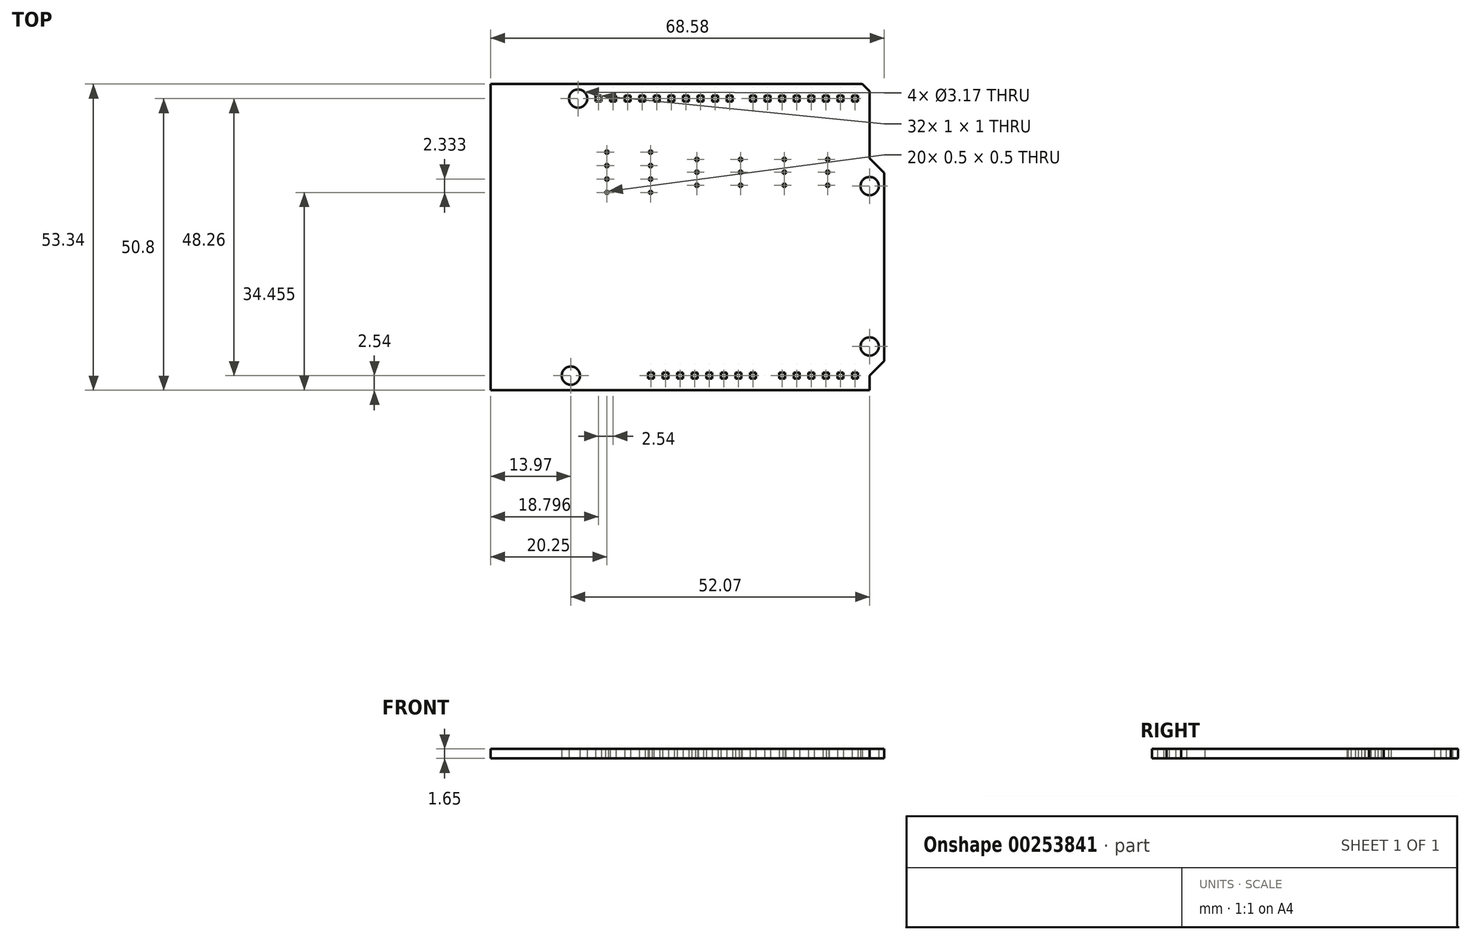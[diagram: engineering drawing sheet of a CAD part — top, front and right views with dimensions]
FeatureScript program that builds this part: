
annotation { "Feature Type Name" : "Feature", "Feature Type Description" : "" }
export const myFeature = defineFeature(function(context is Context, id is Id, definition is map)
    precondition{}
    {
        {
            var Q0;
            Q0=qCreatedBy(makeId("Top.planeOp"),FACE);
            var sketch = newSketch(context, id + "F0", { "sketchPlane" : qUnion([Q0])});
            skLineSegment(sketch, "E0", {"start": v(0, 0) * mm, "end": v(0, 53.34) * mm});
            skLineSegment(sketch, "E1", {"start": v(0, 53.34) * mm, "end": v(64.77, 53.34) * mm});
            skLineSegment(sketch, "E2", {"start": v(66.04, 52.07) * mm, "end": v(66.04, 40.39) * mm});
            skLineSegment(sketch, "E3", {"start": v(68.58, 37.85) * mm, "end": v(68.58, 5.08) * mm});
            skLineSegment(sketch, "E4", {"start": v(66.04, 0) * mm, "end": v(0, 0) * mm});
            skLineSegment(sketch, "E5", {"start": v(66.04, 40.39) * mm, "end": v(68.58, 37.85) * mm});
            skLineSegment(sketch, "E6", {"start": v(68.58, 5.08) * mm, "end": v(66.04, 2.54) * mm});
            skLineSegment(sketch, "E7", {"start": v(66.04, 2.54) * mm, "end": v(66.04, 0) * mm});
            skPoint(sketch, "E8.orphan", {"position": v(68.58, 0) * mm});
            skLineSegment(sketch, "E9", {"start": v(64.77, 53.34) * mm, "end": v(66.04, 52.07) * mm});
            skCircle(sketch, "E10", {"center": v(15.24, 50.8) * mm, "radius": 1.59 * mm});
            skCircle(sketch, "E11", {"center": v(66.04, 35.56) * mm, "radius": 1.59 * mm});
            skCircle(sketch, "E12", {"center": v(13.97, 2.54) * mm, "radius": 1.59 * mm});
            skCircle(sketch, "E13", {"center": v(66.04, 7.62) * mm, "radius": 1.59 * mm});
            skLineSegment(sketch, "E14.bottom", {"start": v(63, 3.04) * mm, "end": v(64, 3.04) * mm});
            skLineSegment(sketch, "E14.top", {"start": v(63, 2.04) * mm, "end": v(64, 2.04) * mm});
            skLineSegment(sketch, "E14.left", {"start": v(63, 3.04) * mm, "end": v(63, 2.04) * mm});
            skLineSegment(sketch, "E14.right", {"start": v(64, 3.04) * mm, "end": v(64, 2.04) * mm});
            skLineSegment(sketch, "E15", {"start": v(66.04, 2.54) * mm, "end": v(0, 2.54) * mm, "construction": true});
            skLineSegment(sketch, "E16.1.0.0", {"start": v(60.46, 3.04) * mm, "end": v(61.46, 3.04) * mm});
            skLineSegment(sketch, "E16.1.0.1", {"start": v(60.46, 3.04) * mm, "end": v(60.46, 2.04) * mm});
            skLineSegment(sketch, "E16.1.0.2", {"start": v(60.46, 2.04) * mm, "end": v(61.46, 2.04) * mm});
            skLineSegment(sketch, "E16.1.0.3", {"start": v(61.46, 3.04) * mm, "end": v(61.46, 2.04) * mm});
            skLineSegment(sketch, "E16.2.0.0", {"start": v(57.92, 3.04) * mm, "end": v(58.92, 3.04) * mm});
            skLineSegment(sketch, "E16.2.0.1", {"start": v(57.92, 3.04) * mm, "end": v(57.92, 2.04) * mm});
            skLineSegment(sketch, "E16.2.0.2", {"start": v(57.92, 2.04) * mm, "end": v(58.92, 2.04) * mm});
            skLineSegment(sketch, "E16.2.0.3", {"start": v(58.92, 3.04) * mm, "end": v(58.92, 2.04) * mm});
            skLineSegment(sketch, "E16.3.0.0", {"start": v(55.38, 3.04) * mm, "end": v(56.38, 3.04) * mm});
            skLineSegment(sketch, "E16.3.0.1", {"start": v(55.38, 3.04) * mm, "end": v(55.38, 2.04) * mm});
            skLineSegment(sketch, "E16.3.0.2", {"start": v(55.38, 2.04) * mm, "end": v(56.38, 2.04) * mm});
            skLineSegment(sketch, "E16.3.0.3", {"start": v(56.38, 3.04) * mm, "end": v(56.38, 2.04) * mm});
            skLineSegment(sketch, "E16.4.0.0", {"start": v(52.84, 3.04) * mm, "end": v(53.84, 3.04) * mm});
            skLineSegment(sketch, "E16.4.0.1", {"start": v(52.84, 3.04) * mm, "end": v(52.84, 2.04) * mm});
            skLineSegment(sketch, "E16.4.0.2", {"start": v(52.84, 2.04) * mm, "end": v(53.84, 2.04) * mm});
            skLineSegment(sketch, "E16.4.0.3", {"start": v(53.84, 3.04) * mm, "end": v(53.84, 2.04) * mm});
            skLineSegment(sketch, "E16.5.0.0", {"start": v(50.3, 3.04) * mm, "end": v(51.3, 3.04) * mm});
            skLineSegment(sketch, "E16.5.0.1", {"start": v(50.3, 3.04) * mm, "end": v(50.3, 2.04) * mm});
            skLineSegment(sketch, "E16.5.0.2", {"start": v(50.3, 2.04) * mm, "end": v(51.3, 2.04) * mm});
            skLineSegment(sketch, "E16.5.0.3", {"start": v(51.3, 3.04) * mm, "end": v(51.3, 2.04) * mm});
            skLineSegment(sketch, "E16.direction1", {"start": v(63, 3.04) * mm, "end": v(60.46, 3.04) * mm, "construction": true});
            skLineSegment(sketch, "E17.bottom", {"start": v(45.22, 3.04) * mm, "end": v(46.22, 3.04) * mm});
            skLineSegment(sketch, "E17.top", {"start": v(45.22, 2.04) * mm, "end": v(46.22, 2.04) * mm});
            skLineSegment(sketch, "E17.left", {"start": v(45.22, 3.04) * mm, "end": v(45.22, 2.04) * mm});
            skLineSegment(sketch, "E17.right", {"start": v(46.22, 3.04) * mm, "end": v(46.22, 2.04) * mm});
            skLineSegment(sketch, "E18.1.0.0", {"start": v(42.68, 3.04) * mm, "end": v(43.68, 3.04) * mm});
            skLineSegment(sketch, "E18.1.0.1", {"start": v(42.68, 3.04) * mm, "end": v(42.68, 2.04) * mm});
            skLineSegment(sketch, "E18.1.0.2", {"start": v(42.68, 2.04) * mm, "end": v(43.68, 2.04) * mm});
            skLineSegment(sketch, "E18.1.0.3", {"start": v(43.68, 3.04) * mm, "end": v(43.68, 2.04) * mm});
            skLineSegment(sketch, "E18.2.0.0", {"start": v(40.14, 3.04) * mm, "end": v(41.14, 3.04) * mm});
            skLineSegment(sketch, "E18.2.0.1", {"start": v(40.14, 3.04) * mm, "end": v(40.14, 2.04) * mm});
            skLineSegment(sketch, "E18.2.0.2", {"start": v(40.14, 2.04) * mm, "end": v(41.14, 2.04) * mm});
            skLineSegment(sketch, "E18.2.0.3", {"start": v(41.14, 3.04) * mm, "end": v(41.14, 2.04) * mm});
            skLineSegment(sketch, "E18.3.0.0", {"start": v(37.6, 3.04) * mm, "end": v(38.6, 3.04) * mm});
            skLineSegment(sketch, "E18.3.0.1", {"start": v(37.6, 3.04) * mm, "end": v(37.6, 2.04) * mm});
            skLineSegment(sketch, "E18.3.0.2", {"start": v(37.6, 2.04) * mm, "end": v(38.6, 2.04) * mm});
            skLineSegment(sketch, "E18.3.0.3", {"start": v(38.6, 3.04) * mm, "end": v(38.6, 2.04) * mm});
            skLineSegment(sketch, "E18.4.0.0", {"start": v(35.06, 3.04) * mm, "end": v(36.06, 3.04) * mm});
            skLineSegment(sketch, "E18.4.0.1", {"start": v(35.06, 3.04) * mm, "end": v(35.06, 2.04) * mm});
            skLineSegment(sketch, "E18.4.0.2", {"start": v(35.06, 2.04) * mm, "end": v(36.06, 2.04) * mm});
            skLineSegment(sketch, "E18.4.0.3", {"start": v(36.06, 3.04) * mm, "end": v(36.06, 2.04) * mm});
            skLineSegment(sketch, "E18.5.0.0", {"start": v(32.52, 3.04) * mm, "end": v(33.52, 3.04) * mm});
            skLineSegment(sketch, "E18.5.0.1", {"start": v(32.52, 3.04) * mm, "end": v(32.52, 2.04) * mm});
            skLineSegment(sketch, "E18.5.0.2", {"start": v(32.52, 2.04) * mm, "end": v(33.52, 2.04) * mm});
            skLineSegment(sketch, "E18.5.0.3", {"start": v(33.52, 3.04) * mm, "end": v(33.52, 2.04) * mm});
            skLineSegment(sketch, "E18.6.0.0", {"start": v(29.98, 3.04) * mm, "end": v(30.98, 3.04) * mm});
            skLineSegment(sketch, "E18.6.0.1", {"start": v(29.98, 3.04) * mm, "end": v(29.98, 2.04) * mm});
            skLineSegment(sketch, "E18.6.0.2", {"start": v(29.98, 2.04) * mm, "end": v(30.98, 2.04) * mm});
            skLineSegment(sketch, "E18.6.0.3", {"start": v(30.98, 3.04) * mm, "end": v(30.98, 2.04) * mm});
            skLineSegment(sketch, "E18.7.0.0", {"start": v(27.44, 3.04) * mm, "end": v(28.44, 3.04) * mm});
            skLineSegment(sketch, "E18.7.0.1", {"start": v(27.44, 3.04) * mm, "end": v(27.44, 2.04) * mm});
            skLineSegment(sketch, "E18.7.0.2", {"start": v(27.44, 2.04) * mm, "end": v(28.44, 2.04) * mm});
            skLineSegment(sketch, "E18.7.0.3", {"start": v(28.44, 3.04) * mm, "end": v(28.44, 2.04) * mm});
            skLineSegment(sketch, "E18.direction1", {"start": v(45.22, 3.04) * mm, "end": v(42.68, 3.04) * mm, "construction": true});
            skLineSegment(sketch, "E19", {"start": v(66.04, 50.8) * mm, "end": v(0, 50.8) * mm, "construction": true});
            skLineSegment(sketch, "E20.bottom", {"start": v(63, 51.3) * mm, "end": v(64, 51.3) * mm});
            skLineSegment(sketch, "E20.top", {"start": v(63, 50.3) * mm, "end": v(64, 50.3) * mm});
            skLineSegment(sketch, "E20.left", {"start": v(63, 51.3) * mm, "end": v(63, 50.3) * mm});
            skLineSegment(sketch, "E20.right", {"start": v(64, 51.3) * mm, "end": v(64, 50.3) * mm});
            skLineSegment(sketch, "E21.1.0.0", {"start": v(60.46, 51.3) * mm, "end": v(60.46, 50.3) * mm});
            skLineSegment(sketch, "E21.1.0.1", {"start": v(60.46, 51.3) * mm, "end": v(61.46, 51.3) * mm});
            skLineSegment(sketch, "E21.1.0.2", {"start": v(61.46, 51.3) * mm, "end": v(61.46, 50.3) * mm});
            skLineSegment(sketch, "E21.1.0.3", {"start": v(60.46, 50.3) * mm, "end": v(61.46, 50.3) * mm});
            skLineSegment(sketch, "E21.2.0.0", {"start": v(57.92, 51.3) * mm, "end": v(57.92, 50.3) * mm});
            skLineSegment(sketch, "E21.2.0.1", {"start": v(57.92, 51.3) * mm, "end": v(58.92, 51.3) * mm});
            skLineSegment(sketch, "E21.2.0.2", {"start": v(58.92, 51.3) * mm, "end": v(58.92, 50.3) * mm});
            skLineSegment(sketch, "E21.2.0.3", {"start": v(57.92, 50.3) * mm, "end": v(58.92, 50.3) * mm});
            skLineSegment(sketch, "E21.3.0.0", {"start": v(55.38, 51.3) * mm, "end": v(55.38, 50.3) * mm});
            skLineSegment(sketch, "E21.3.0.1", {"start": v(55.38, 51.3) * mm, "end": v(56.38, 51.3) * mm});
            skLineSegment(sketch, "E21.3.0.2", {"start": v(56.38, 51.3) * mm, "end": v(56.38, 50.3) * mm});
            skLineSegment(sketch, "E21.3.0.3", {"start": v(55.38, 50.3) * mm, "end": v(56.38, 50.3) * mm});
            skLineSegment(sketch, "E21.4.0.0", {"start": v(52.84, 51.3) * mm, "end": v(52.84, 50.3) * mm});
            skLineSegment(sketch, "E21.4.0.1", {"start": v(52.84, 51.3) * mm, "end": v(53.84, 51.3) * mm});
            skLineSegment(sketch, "E21.4.0.2", {"start": v(53.84, 51.3) * mm, "end": v(53.84, 50.3) * mm});
            skLineSegment(sketch, "E21.4.0.3", {"start": v(52.84, 50.3) * mm, "end": v(53.84, 50.3) * mm});
            skLineSegment(sketch, "E21.5.0.0", {"start": v(50.3, 51.3) * mm, "end": v(50.3, 50.3) * mm});
            skLineSegment(sketch, "E21.5.0.1", {"start": v(50.3, 51.3) * mm, "end": v(51.3, 51.3) * mm});
            skLineSegment(sketch, "E21.5.0.2", {"start": v(51.3, 51.3) * mm, "end": v(51.3, 50.3) * mm});
            skLineSegment(sketch, "E21.5.0.3", {"start": v(50.3, 50.3) * mm, "end": v(51.3, 50.3) * mm});
            skLineSegment(sketch, "E21.6.0.0", {"start": v(47.76, 51.3) * mm, "end": v(47.76, 50.3) * mm});
            skLineSegment(sketch, "E21.6.0.1", {"start": v(47.76, 51.3) * mm, "end": v(48.76, 51.3) * mm});
            skLineSegment(sketch, "E21.6.0.2", {"start": v(48.76, 51.3) * mm, "end": v(48.76, 50.3) * mm});
            skLineSegment(sketch, "E21.6.0.3", {"start": v(47.76, 50.3) * mm, "end": v(48.76, 50.3) * mm});
            skLineSegment(sketch, "E21.7.0.0", {"start": v(45.22, 51.3) * mm, "end": v(45.22, 50.3) * mm});
            skLineSegment(sketch, "E21.7.0.1", {"start": v(45.22, 51.3) * mm, "end": v(46.22, 51.3) * mm});
            skLineSegment(sketch, "E21.7.0.2", {"start": v(46.22, 51.3) * mm, "end": v(46.22, 50.3) * mm});
            skLineSegment(sketch, "E21.7.0.3", {"start": v(45.22, 50.3) * mm, "end": v(46.22, 50.3) * mm});
            skLineSegment(sketch, "E21.direction1", {"start": v(63, 50.3) * mm, "end": v(60.46, 50.3) * mm, "construction": true});
            skLineSegment(sketch, "E22.bottom", {"start": v(41.16, 51.3) * mm, "end": v(42.16, 51.3) * mm});
            skLineSegment(sketch, "E22.top", {"start": v(41.16, 50.3) * mm, "end": v(42.16, 50.3) * mm});
            skLineSegment(sketch, "E22.left", {"start": v(41.16, 51.3) * mm, "end": v(41.16, 50.3) * mm});
            skLineSegment(sketch, "E22.right", {"start": v(42.16, 51.3) * mm, "end": v(42.16, 50.3) * mm});
            skLineSegment(sketch, "E23.1.0.0", {"start": v(38.62, 51.3) * mm, "end": v(39.62, 51.3) * mm});
            skLineSegment(sketch, "E23.1.0.1", {"start": v(38.62, 51.3) * mm, "end": v(38.62, 50.3) * mm});
            skLineSegment(sketch, "E23.1.0.2", {"start": v(38.62, 50.3) * mm, "end": v(39.62, 50.3) * mm});
            skLineSegment(sketch, "E23.1.0.3", {"start": v(39.62, 51.3) * mm, "end": v(39.62, 50.3) * mm});
            skLineSegment(sketch, "E23.2.0.0", {"start": v(36.08, 51.3) * mm, "end": v(37.08, 51.3) * mm});
            skLineSegment(sketch, "E23.2.0.1", {"start": v(36.08, 51.3) * mm, "end": v(36.08, 50.3) * mm});
            skLineSegment(sketch, "E23.2.0.2", {"start": v(36.08, 50.3) * mm, "end": v(37.08, 50.3) * mm});
            skLineSegment(sketch, "E23.2.0.3", {"start": v(37.08, 51.3) * mm, "end": v(37.08, 50.3) * mm});
            skLineSegment(sketch, "E23.3.0.0", {"start": v(33.54, 51.3) * mm, "end": v(34.54, 51.3) * mm});
            skLineSegment(sketch, "E23.3.0.1", {"start": v(33.54, 51.3) * mm, "end": v(33.54, 50.3) * mm});
            skLineSegment(sketch, "E23.3.0.2", {"start": v(33.54, 50.3) * mm, "end": v(34.54, 50.3) * mm});
            skLineSegment(sketch, "E23.3.0.3", {"start": v(34.54, 51.3) * mm, "end": v(34.54, 50.3) * mm});
            skLineSegment(sketch, "E23.4.0.0", {"start": v(31, 51.3) * mm, "end": v(32, 51.3) * mm});
            skLineSegment(sketch, "E23.4.0.1", {"start": v(31, 51.3) * mm, "end": v(31, 50.3) * mm});
            skLineSegment(sketch, "E23.4.0.2", {"start": v(31, 50.3) * mm, "end": v(32, 50.3) * mm});
            skLineSegment(sketch, "E23.4.0.3", {"start": v(32, 51.3) * mm, "end": v(32, 50.3) * mm});
            skLineSegment(sketch, "E23.5.0.0", {"start": v(28.46, 51.3) * mm, "end": v(29.46, 51.3) * mm});
            skLineSegment(sketch, "E23.5.0.1", {"start": v(28.46, 51.3) * mm, "end": v(28.46, 50.3) * mm});
            skLineSegment(sketch, "E23.5.0.2", {"start": v(28.46, 50.3) * mm, "end": v(29.46, 50.3) * mm});
            skLineSegment(sketch, "E23.5.0.3", {"start": v(29.46, 51.3) * mm, "end": v(29.46, 50.3) * mm});
            skLineSegment(sketch, "E23.6.0.0", {"start": v(25.92, 51.3) * mm, "end": v(26.92, 51.3) * mm});
            skLineSegment(sketch, "E23.6.0.1", {"start": v(25.92, 51.3) * mm, "end": v(25.92, 50.3) * mm});
            skLineSegment(sketch, "E23.6.0.2", {"start": v(25.92, 50.3) * mm, "end": v(26.92, 50.3) * mm});
            skLineSegment(sketch, "E23.6.0.3", {"start": v(26.92, 51.3) * mm, "end": v(26.92, 50.3) * mm});
            skLineSegment(sketch, "E23.7.0.0", {"start": v(23.38, 51.3) * mm, "end": v(24.38, 51.3) * mm});
            skLineSegment(sketch, "E23.7.0.1", {"start": v(23.38, 51.3) * mm, "end": v(23.38, 50.3) * mm});
            skLineSegment(sketch, "E23.7.0.2", {"start": v(23.38, 50.3) * mm, "end": v(24.38, 50.3) * mm});
            skLineSegment(sketch, "E23.7.0.3", {"start": v(24.38, 51.3) * mm, "end": v(24.38, 50.3) * mm});
            skLineSegment(sketch, "E23.8.0.0", {"start": v(20.84, 51.3) * mm, "end": v(21.84, 51.3) * mm});
            skLineSegment(sketch, "E23.8.0.1", {"start": v(20.84, 51.3) * mm, "end": v(20.84, 50.3) * mm});
            skLineSegment(sketch, "E23.8.0.2", {"start": v(20.84, 50.3) * mm, "end": v(21.84, 50.3) * mm});
            skLineSegment(sketch, "E23.8.0.3", {"start": v(21.84, 51.3) * mm, "end": v(21.84, 50.3) * mm});
            skLineSegment(sketch, "E23.9.0.0", {"start": v(18.3, 51.3) * mm, "end": v(19.3, 51.3) * mm});
            skLineSegment(sketch, "E23.9.0.1", {"start": v(18.3, 51.3) * mm, "end": v(18.3, 50.3) * mm});
            skLineSegment(sketch, "E23.9.0.2", {"start": v(18.3, 50.3) * mm, "end": v(19.3, 50.3) * mm});
            skLineSegment(sketch, "E23.9.0.3", {"start": v(19.3, 51.3) * mm, "end": v(19.3, 50.3) * mm});
            skLineSegment(sketch, "E23.direction1", {"start": v(41.16, 51.3) * mm, "end": v(38.62, 51.3) * mm, "construction": true});
            skLineSegment(sketch, "E24.bottom", {"start": v(55, 41.7) * mm, "end": v(61, 41.7) * mm, "construction": true});
            skLineSegment(sketch, "E24.top", {"start": v(55, 34.2) * mm, "end": v(61, 34.2) * mm, "construction": true});
            skLineSegment(sketch, "E24.left", {"start": v(55, 41.7) * mm, "end": v(55, 34.2) * mm, "construction": true});
            skLineSegment(sketch, "E24.right", {"start": v(61, 41.7) * mm, "end": v(61, 34.2) * mm, "construction": true});
            skLineSegment(sketch, "E25.bottom", {"start": v(58.5, 40.46) * mm, "end": v(59, 40.46) * mm});
            skLineSegment(sketch, "E25.top", {"start": v(58.5, 35.46) * mm, "end": v(59, 35.46) * mm});
            skLineSegment(sketch, "E25.left", {"start": v(58.5, 40.46) * mm, "end": v(58.5, 39.96) * mm});
            skLineSegment(sketch, "E25.right", {"start": v(59, 40.46) * mm, "end": v(59, 39.96) * mm});
            skLineSegment(sketch, "E26", {"start": v(58.5, 39.96) * mm, "end": v(59, 39.96) * mm});
            skLineSegment(sketch, "E27", {"start": v(58.5, 38.2) * mm, "end": v(59, 38.2) * mm});
            skLineSegment(sketch, "E28", {"start": v(58.5, 37.7) * mm, "end": v(59, 37.7) * mm});
            skLineSegment(sketch, "E29", {"start": v(58.5, 35.96) * mm, "end": v(59, 35.96) * mm});
            skLineSegment(sketch, "E30.trimOffspring", {"start": v(58.5, 38.2) * mm, "end": v(58.5, 37.7) * mm});
            skLineSegment(sketch, "E31.trimOffspring", {"start": v(59, 38.2) * mm, "end": v(59, 37.7) * mm});
            skLineSegment(sketch, "E32.trimOffspring", {"start": v(58.5, 35.96) * mm, "end": v(58.5, 35.46) * mm});
            skLineSegment(sketch, "E33.trimOffspring", {"start": v(59, 35.96) * mm, "end": v(59, 35.46) * mm});
            skLineSegment(sketch, "E34", {"start": v(55, 37.96) * mm, "end": v(61, 37.96) * mm, "construction": true});
            skLineSegment(sketch, "E35.1.0.0", {"start": v(50.9, 40.46) * mm, "end": v(51.4, 40.46) * mm});
            skLineSegment(sketch, "E35.1.0.1", {"start": v(50.9, 40.46) * mm, "end": v(50.9, 39.96) * mm});
            skLineSegment(sketch, "E35.1.0.2", {"start": v(50.9, 39.96) * mm, "end": v(51.4, 39.96) * mm});
            skLineSegment(sketch, "E35.1.0.3", {"start": v(51.4, 40.46) * mm, "end": v(51.4, 39.96) * mm});
            skLineSegment(sketch, "E35.1.0.4", {"start": v(50.9, 38.2) * mm, "end": v(51.4, 38.2) * mm});
            skLineSegment(sketch, "E35.1.0.5", {"start": v(50.9, 38.2) * mm, "end": v(50.9, 37.7) * mm});
            skLineSegment(sketch, "E35.1.0.6", {"start": v(51.4, 38.2) * mm, "end": v(51.4, 37.7) * mm});
            skLineSegment(sketch, "E35.1.0.7", {"start": v(50.9, 37.7) * mm, "end": v(51.4, 37.7) * mm});
            skLineSegment(sketch, "E35.1.0.8", {"start": v(50.9, 35.96) * mm, "end": v(51.4, 35.96) * mm});
            skLineSegment(sketch, "E35.1.0.9", {"start": v(50.9, 35.96) * mm, "end": v(50.9, 35.46) * mm});
            skLineSegment(sketch, "E35.1.0.10", {"start": v(50.9, 35.46) * mm, "end": v(51.4, 35.46) * mm});
            skLineSegment(sketch, "E35.1.0.11", {"start": v(51.4, 35.96) * mm, "end": v(51.4, 35.46) * mm});
            skLineSegment(sketch, "E35.2.0.0", {"start": v(43.3, 40.46) * mm, "end": v(43.8, 40.46) * mm});
            skLineSegment(sketch, "E35.2.0.1", {"start": v(43.3, 40.46) * mm, "end": v(43.3, 39.96) * mm});
            skLineSegment(sketch, "E35.2.0.2", {"start": v(43.3, 39.96) * mm, "end": v(43.8, 39.96) * mm});
            skLineSegment(sketch, "E35.2.0.3", {"start": v(43.8, 40.46) * mm, "end": v(43.8, 39.96) * mm});
            skLineSegment(sketch, "E35.2.0.4", {"start": v(43.3, 38.2) * mm, "end": v(43.8, 38.2) * mm});
            skLineSegment(sketch, "E35.2.0.5", {"start": v(43.3, 38.2) * mm, "end": v(43.3, 37.7) * mm});
            skLineSegment(sketch, "E35.2.0.6", {"start": v(43.8, 38.2) * mm, "end": v(43.8, 37.7) * mm});
            skLineSegment(sketch, "E35.2.0.7", {"start": v(43.3, 37.7) * mm, "end": v(43.8, 37.7) * mm});
            skLineSegment(sketch, "E35.2.0.8", {"start": v(43.3, 35.96) * mm, "end": v(43.8, 35.96) * mm});
            skLineSegment(sketch, "E35.2.0.9", {"start": v(43.3, 35.96) * mm, "end": v(43.3, 35.46) * mm});
            skLineSegment(sketch, "E35.2.0.10", {"start": v(43.3, 35.46) * mm, "end": v(43.8, 35.46) * mm});
            skLineSegment(sketch, "E35.2.0.11", {"start": v(43.8, 35.96) * mm, "end": v(43.8, 35.46) * mm});
            skLineSegment(sketch, "E35.3.0.0", {"start": v(35.7, 40.46) * mm, "end": v(36.2, 40.46) * mm});
            skLineSegment(sketch, "E35.3.0.1", {"start": v(35.7, 40.46) * mm, "end": v(35.7, 39.96) * mm});
            skLineSegment(sketch, "E35.3.0.2", {"start": v(35.7, 39.96) * mm, "end": v(36.2, 39.96) * mm});
            skLineSegment(sketch, "E35.3.0.3", {"start": v(36.2, 40.46) * mm, "end": v(36.2, 39.96) * mm});
            skLineSegment(sketch, "E35.3.0.4", {"start": v(35.7, 38.2) * mm, "end": v(36.2, 38.2) * mm});
            skLineSegment(sketch, "E35.3.0.5", {"start": v(35.7, 38.2) * mm, "end": v(35.7, 37.7) * mm});
            skLineSegment(sketch, "E35.3.0.6", {"start": v(36.2, 38.2) * mm, "end": v(36.2, 37.7) * mm});
            skLineSegment(sketch, "E35.3.0.7", {"start": v(35.7, 37.7) * mm, "end": v(36.2, 37.7) * mm});
            skLineSegment(sketch, "E35.3.0.8", {"start": v(35.7, 35.96) * mm, "end": v(36.2, 35.96) * mm});
            skLineSegment(sketch, "E35.3.0.9", {"start": v(35.7, 35.96) * mm, "end": v(35.7, 35.46) * mm});
            skLineSegment(sketch, "E35.3.0.10", {"start": v(35.7, 35.46) * mm, "end": v(36.2, 35.46) * mm});
            skLineSegment(sketch, "E35.3.0.11", {"start": v(36.2, 35.96) * mm, "end": v(36.2, 35.46) * mm});
            skLineSegment(sketch, "E35.direction1", {"start": v(58.5, 40.46) * mm, "end": v(50.9, 40.46) * mm, "construction": true});
            skLineSegment(sketch, "E36.bottom", {"start": v(27.6, 41.7) * mm, "end": v(28.1, 41.7) * mm});
            skLineSegment(sketch, "E36.top", {"start": v(27.6, 34.2) * mm, "end": v(28.1, 34.2) * mm});
            skLineSegment(sketch, "E36.left", {"start": v(27.6, 41.7) * mm, "end": v(27.6, 41.2) * mm});
            skLineSegment(sketch, "E36.right", {"start": v(28.1, 41.7) * mm, "end": v(28.1, 41.2) * mm});
            skLineSegment(sketch, "E37", {"start": v(27.6, 41.2) * mm, "end": v(28.1, 41.2) * mm});
            skLineSegment(sketch, "E38", {"start": v(27.6, 34.7) * mm, "end": v(28.1, 34.7) * mm});
            skLineSegment(sketch, "E39", {"start": v(27.6, 39.37) * mm, "end": v(28.1, 39.37) * mm});
            skLineSegment(sketch, "E40", {"start": v(27.6, 38.87) * mm, "end": v(28.1, 38.87) * mm});
            skLineSegment(sketch, "E41", {"start": v(27.6, 37.04) * mm, "end": v(28.1, 37.04) * mm});
            skLineSegment(sketch, "E42", {"start": v(27.6, 36.54) * mm, "end": v(28.1, 36.54) * mm});
            skLineSegment(sketch, "E43.trimOffspring", {"start": v(27.6, 39.37) * mm, "end": v(27.6, 38.87) * mm});
            skLineSegment(sketch, "E44.trimOffspring", {"start": v(28.1, 39.37) * mm, "end": v(28.1, 38.87) * mm});
            skLineSegment(sketch, "E45.trimOffspring", {"start": v(27.6, 37.04) * mm, "end": v(27.6, 36.54) * mm});
            skLineSegment(sketch, "E46.trimOffspring", {"start": v(28.1, 37.04) * mm, "end": v(28.1, 36.54) * mm});
            skLineSegment(sketch, "E47.trimOffspring", {"start": v(27.6, 34.7) * mm, "end": v(27.6, 34.2) * mm});
            skLineSegment(sketch, "E48.trimOffspring", {"start": v(28.1, 34.7) * mm, "end": v(28.1, 34.2) * mm});
            skLineSegment(sketch, "E49", {"start": v(35.7, 37.96) * mm, "end": v(0, 37.96) * mm, "construction": true});
            skLineSegment(sketch, "E50.bottom", {"start": v(20, 41.7) * mm, "end": v(20.5, 41.7) * mm});
            skLineSegment(sketch, "E50.top", {"start": v(20, 34.2) * mm, "end": v(20.5, 34.2) * mm});
            skLineSegment(sketch, "E50.left", {"start": v(20, 41.7) * mm, "end": v(20, 41.2) * mm});
            skLineSegment(sketch, "E50.right", {"start": v(20.5, 41.7) * mm, "end": v(20.5, 41.2) * mm});
            skLineSegment(sketch, "E51", {"start": v(20, 41.2) * mm, "end": v(20.5, 41.2) * mm});
            skLineSegment(sketch, "E52", {"start": v(20, 39.37) * mm, "end": v(20.5, 39.37) * mm});
            skLineSegment(sketch, "E53", {"start": v(20, 38.87) * mm, "end": v(20.5, 38.87) * mm});
            skLineSegment(sketch, "E54", {"start": v(20, 37.04) * mm, "end": v(20.5, 37.04) * mm});
            skLineSegment(sketch, "E55", {"start": v(20, 36.54) * mm, "end": v(20.5, 36.54) * mm});
            skLineSegment(sketch, "E56", {"start": v(20, 34.7) * mm, "end": v(20.5, 34.7) * mm});
            skLineSegment(sketch, "E57.trimOffspring", {"start": v(20, 39.37) * mm, "end": v(20, 38.87) * mm});
            skLineSegment(sketch, "E58.trimOffspring", {"start": v(20.5, 39.37) * mm, "end": v(20.5, 38.87) * mm});
            skLineSegment(sketch, "E59.trimOffspring", {"start": v(20, 37.04) * mm, "end": v(20, 36.54) * mm});
            skLineSegment(sketch, "E60.trimOffspring", {"start": v(20.5, 37.04) * mm, "end": v(20.5, 36.54) * mm});
            skLineSegment(sketch, "E61.trimOffspring", {"start": v(20, 34.7) * mm, "end": v(20, 34.2) * mm});
            skLineSegment(sketch, "E62.trimOffspring", {"start": v(20.5, 34.7) * mm, "end": v(20.5, 34.2) * mm});
            skSolve(sketch);
        }
        {
            var Q0;
            Q0=makeQuery(id+"F0.imprint","IMPRINT",FACE,{"disambiguationData":[TD([[makeQuery(id+"F0.imprint","IMPRINT",EDGE,{"derivedFrom":sQuery(id+"F0.wireOp",EDGE,"E0")}),-1.0]])]});
            extrude(context, id + "F1", {"entities" : qUnion([Q0]), "depth" : 1.65 * mm});
        }
    });
